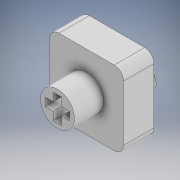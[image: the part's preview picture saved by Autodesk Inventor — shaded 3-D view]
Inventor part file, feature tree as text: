
AUTODESK INVENTOR PART (.ipt)
format: ipt  version: 2022 (Build 260153000, 153)  size: 274,944 bytes
history: native  units: in
note: dims shown in document units (in); Inventor stores cm internally (conversion verified against a paired STEP export)
features: sketch x4, extrude x3, plane x1, projected_geometry x1
ambient origin geometry x8: Origin, YZ Plane, XZ Plane, XY Plane, X Axis, Y Axis, Z Axis, Center Point
bodies: Body1 (feature_tree)
feature tree (9):
  sketch  "Sketch1"  dims[d3=0.2205in d4=0.1594in]
  plane  "Work Plane1"
  sketch  "Sketch2"  dims[d5=0.0531in d6=0.1594in]
  extrude  "Extrusion3"  Depth=0.1594in
  extrude  "Extrusion4"  Depth=0.1594in
  extrude  "Extrusion5"  Depth=0.5016in
  projected_geometry  "Projected Loop1"
  sketch  "Sketch3"  dims[d7=0.0531in d10=0.5016in]
  sketch  "Sketch4"  dims[d12=0.1969in d13=0.0in d14=0.2205in d15=0.1594in d16=0.0531in d17=0.1594in d18=0.0531in d19=0.189in d20=0.0in d21=0.0892in d22=0.2693in d23=0.0354in d24=0.0in]
